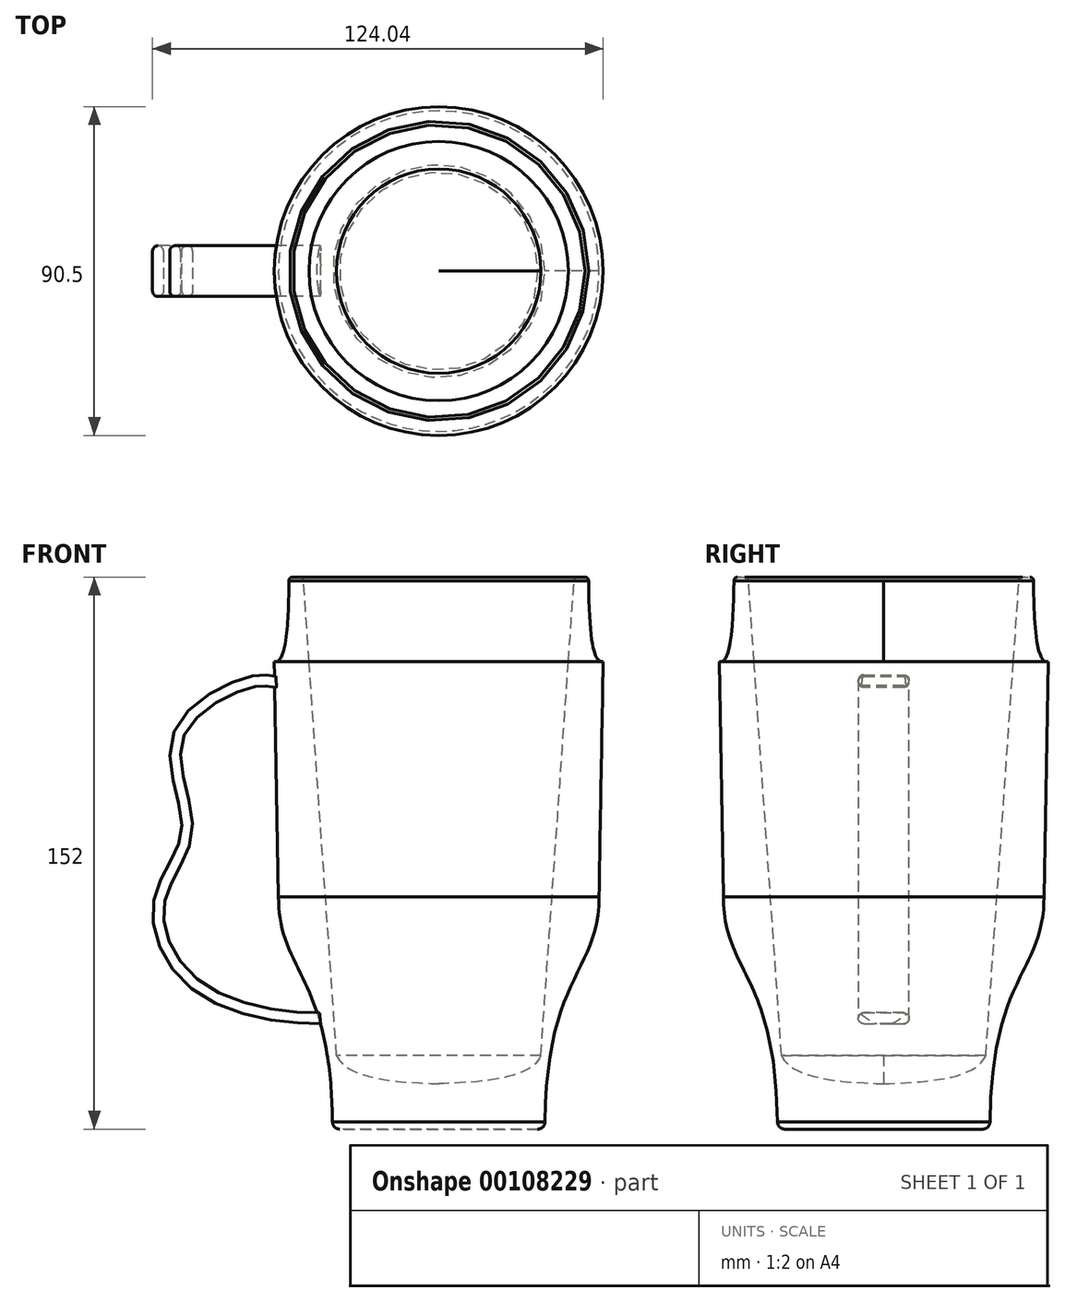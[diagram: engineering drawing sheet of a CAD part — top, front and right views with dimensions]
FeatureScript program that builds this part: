
annotation { "Feature Type Name" : "Feature", "Feature Type Description" : "" }
export const myFeature = defineFeature(function(context is Context, id is Id, definition is map)
    precondition{}
    {
        {
            var Q0;
            Q0=qCreatedBy(makeId("Top.planeOp"),FACE);
            var sketch = newSketch(context, id + "F0", { "sketchPlane" : qUnion([Q0])});
            skCircle(sketch, "E0", {"center": v(0, 0) * mm, "radius": 41.25 * mm});
            skCircle(sketch, "E1", {"center": v(0, 0) * mm, "radius": 45.25 * mm, "construction": true});
            skCircle(sketch, "E2", {"center": v(0, 0) * mm, "radius": 29.25 * mm, "construction": true});
            skCircle(sketch, "E3", {"center": v(0, 0) * mm, "radius": 44.12 * mm, "construction": true});
            skSolve(sketch);
        }
        {
            var Q0;
            Q0=qCreatedBy(makeId("Top.planeOp"),FACE);
            cPlane(context, id + "F1", {"entities" : qUnion([Q0]), "cplaneType" : CPlaneType.OFFSET, "offset" : 23.3 * mm, "oppositeDirection" : true, "width" : 150 * mm, "height" : 150 * mm});
        }
        {
            var Q0;
            Q0=qCreatedBy(makeId("Top.planeOp"),FACE);
            cPlane(context, id + "F2", {"entities" : qUnion([Q0]), "cplaneType" : CPlaneType.OFFSET, "offset" : 88 * mm, "oppositeDirection" : true, "width" : 150 * mm, "height" : 150 * mm});
        }
        {
            var Q0;
            Q0=qCreatedBy(makeId("Top.planeOp"),FACE);
            cPlane(context, id + "F3", {"entities" : qUnion([Q0]), "cplaneType" : CPlaneType.OFFSET, "offset" : 152 * mm, "oppositeDirection" : true, "width" : 150 * mm, "height" : 150 * mm});
        }
        {
            var Q0;
            Q0=qCreatedBy(id+"F3.planeOp",FACE);
            var sketch = newSketch(context, id + "F4", { "sketchPlane" : qUnion([Q0])});
            skCircle(sketch, "E4", {"center": v(0, 0) * mm, "radius": 29.25 * mm});
            skSolve(sketch);
        }
        {
            var Q0;
            Q0=qCreatedBy(id+"F2.planeOp",FACE);
            var sketch = newSketch(context, id + "F5", { "sketchPlane" : qUnion([Q0])});
            skCircle(sketch, "E5", {"center": v(0, 0) * mm, "radius": 44.12 * mm});
            skSolve(sketch);
        }
        {
            var Q0;
            Q0=qCreatedBy(id+"F1.planeOp",FACE);
            var sketch = newSketch(context, id + "F6", { "sketchPlane" : qUnion([Q0])});
            skCircle(sketch, "E6", {"center": v(0, 0) * mm, "radius": 45.25 * mm});
            skSolve(sketch);
        }
        {
            var Q0;
            Q0=makeQuery(id+"F0.imprint","IMPRINT",FACE,{"disambiguationData":[TD([[makeQuery(id+"F0.imprint","IMPRINT",EDGE,{"derivedFrom":sQuery(id+"F0.wireOp",EDGE,"E0")}),1.0]])]});
            var Q1;
            Q1=makeQuery(id+"F6.imprint","IMPRINT",FACE,{"disambiguationData":[TD([[makeQuery(id+"F6.imprint","IMPRINT",EDGE,{"derivedFrom":sQuery(id+"F6.wireOp",EDGE,"E6")}),1.0]])]});
            loft(context, id + "F7", {"startCondition" : LoftEndDerivativeType.NORMAL_TO_PROFILE, "startMagnitude" : 3, "endCondition" : LoftEndDerivativeType.TANGENT_TO_PROFILE, "endMagnitude" : 1, "sheetProfilesArray" : [{ "sheetProfileEntities" : qUnion([Q0]) }, { "sheetProfileEntities" : qUnion([Q1]) }]});
        }
        {
            var Q0;
            Q0=makeQuery(id+"F6.imprint","IMPRINT",FACE,{"disambiguationData":[TD([[makeQuery(id+"F6.imprint","IMPRINT",EDGE,{"derivedFrom":sQuery(id+"F6.wireOp",EDGE,"E6")}),1.0]])]});
            var Q1;
            Q1=makeQuery(id+"F5.imprint","IMPRINT",FACE,{"disambiguationData":[TD([[makeQuery(id+"F5.imprint","IMPRINT",EDGE,{"derivedFrom":sQuery(id+"F5.wireOp",EDGE,"E5")}),1.0]])]});
            loft(context, id + "F8", {"sheetProfilesArray" : [{ "sheetProfileEntities" : qUnion([Q0]) }, { "sheetProfileEntities" : qUnion([Q1]) }]});
        }
        {
            var Q0;
            Q0=makeQuery(id+"F5.imprint","IMPRINT",FACE,{"disambiguationData":[TD([[makeQuery(id+"F5.imprint","IMPRINT",EDGE,{"derivedFrom":sQuery(id+"F5.wireOp",EDGE,"E5")}),1.0]])]});
            var Q1;
            Q1=makeQuery(id+"F4.imprint","IMPRINT",FACE,{"disambiguationData":[TD([[makeQuery(id+"F4.imprint","IMPRINT",EDGE,{"derivedFrom":sQuery(id+"F4.wireOp",EDGE,"E4")}),1.0]])]});
            loft(context, id + "F9", {"operationType" : NewBodyOperationType.ADD, "startCondition" : LoftEndDerivativeType.NORMAL_TO_PROFILE, "startMagnitude" : 1, "endCondition" : LoftEndDerivativeType.NORMAL_TO_PROFILE, "endMagnitude" : 2, "sheetProfilesArray" : [{ "sheetProfileEntities" : qUnion([Q0]) }, { "sheetProfileEntities" : qUnion([Q1]) }]});
        }
        {
            var Q0;
            Q0=qCreatedBy(makeId("Right.planeOp"),FACE);
            cPlane(context, id + "F10", {"entities" : qUnion([Q0]), "cplaneType" : CPlaneType.OFFSET, "offset" : 45 * mm, "oppositeDirection" : true, "width" : 150 * mm, "height" : 150 * mm});
        }
        {
            var Q0;
            Q0=qCreatedBy(id+"F10.planeOp",FACE);
            var sketch = newSketch(context, id + "F11", { "sketchPlane" : qUnion([Q0])});
            skLineSegment(sketch, "E7.bottom", {"start": v(-5.5, -30.36) * mm, "end": v(5.5, -30.36) * mm});
            skLineSegment(sketch, "E7.top", {"start": v(-5.5, -27.36) * mm, "end": v(5.5, -27.36) * mm});
            skPoint(sketch, "E7.middle", {"position": v(0, -28.86) * mm});
            skArc(sketch, "E8", {"start": v(-5.5, -27.36) * mm, "mid": v(-7, -28.86) * mm, "end": v(-5.5, -30.36) * mm});
            skArc(sketch, "E9", {"start": v(5.5, -30.36) * mm, "mid": v(7, -28.86) * mm, "end": v(5.5, -27.36) * mm});
            skSolve(sketch);
        }
        {
            var Q0;
            Q0=qCreatedBy(makeId("Front.planeOp"),FACE);
            var sketch = newSketch(context, id + "F12", { "sketchPlane" : qUnion([Q0])});
            skFitSpline(sketch, "E10", {"points": [v(-44.75, -28.71) * mm, v(-50.54, -28.4) * mm, v(-71.8, -43.33) * mm, v(-69.46, -69.7) * mm, v(-77.15, -89.2) * mm, v(-66.15, -113.07) * mm, v(-32.64, -121.63) * mm], "startDerivative": vector(-59.53, 2.88) * mm, "endDerivative": vector(125.85, 1.87) * mm});
            skSolve(sketch);
        }
        {
            var Q0;
            Q0=makeQuery(id+"F11.imprint","IMPRINT",FACE,{"disambiguationData":[TD([[makeQuery(id+"F11.imprint","IMPRINT",EDGE,{"derivedFrom":sQuery(id+"F11.wireOp",EDGE,"E7.bottom")}),1.0]])]});
            var Q1;
            Q1=sQuery(id+"F12.wireOp",EDGE,"E10");
            sweep(context, id + "F13", {"operationType" : NewBodyOperationType.ADD, "profiles" : qUnion([Q0]), "path" : qUnion([Q1])});
        }
        {
            var Q0;
            Q0=qCreatedBy(makeId("Front.planeOp"),FACE);
            var sketch = newSketch(context, id + "F14", { "sketchPlane" : qUnion([Q0])});
            skFitSpline(sketch, "E11", {"points": [v(28.13, -131.68) * mm, v(0, -139.48) * mm], "startDerivative": vector(-7.7, -20) * mm, "endDerivative": vector(-32.37, -0.92) * mm});
            skLineSegment(sketch, "E12", {"start": v(0, -139.48) * mm, "end": v(0, 3.27) * mm});
            skLineSegment(sketch, "E13", {"start": v(0, 3.27) * mm, "end": v(37.55, 3.27) * mm});
            skLineSegment(sketch, "E14", {"start": v(37.55, 3.27) * mm, "end": v(28.13, -131.68) * mm});
            skSolve(sketch);
        }
        {
            var Q0;
            Q0=qSketchRegion(id+"F14",true);
            var Q1;
            Q1=sQuery(id+"F14.wireOp",EDGE,"E12");
            revolve(context, id + "F15", {"operationType" : NewBodyOperationType.REMOVE, "entities" : qUnion([Q0]), "axis" : qUnion([Q1]), "revolveType" : RevolveType.FULL, "oppositeDirection" : true});
        }
        {
            var Q0;
            Q0=makeQuery(id+"F7.opLoft","MID_CAP_EDGE",EDGE,{"disambiguationData":[OSD([sQuery(id+"F0.wireOp",EDGE,"E0")])],"capPos":0.0});
            var Q1;
            Q1=makeQuery(id+"F15.boolean.opBoolean","INTERSECT",EDGE,{"derivedFrom":[makeQuery(id+"F7.opLoft","CAP_FACE",FACE,{"disambiguationData":[OSD([makeQuery(id+"F0.imprint","IMPRINT",FACE,{"disambiguationData":[TD([[makeQuery(id+"F0.imprint","IMPRINT",EDGE,{"derivedFrom":sQuery(id+"F0.wireOp",EDGE,"E0")}),1.0]])]})])],"isStart":true}),makeQuery(id+"F15.opRevolve","SWEPT_FACE",FACE,{"disambiguationData":[OSD([sQuery(id+"F14.wireOp",EDGE,"E14")])]})]});
            fillet(context, id + "F16", {"entities" : qUnion([Q0, Q1]), "radius" : 1 * mm, "tangentPropagation" : true, "allowEdgeOverflow" : false});
        }
        {
            var Q0;
            Q0=makeQuery(id+"F9.opLoft","MID_CAP_EDGE",EDGE,{"disambiguationData":[OSD([sQuery(id+"F4.wireOp",EDGE,"E4"),sQuery(id+"F5.wireOp",EDGE,"E5")])],"capPos":1.0});
            fillet(context, id + "F17", {"entities" : qUnion([Q0]), "radius" : 2 * mm, "tangentPropagation" : true, "allowEdgeOverflow" : false});
        }
    });
